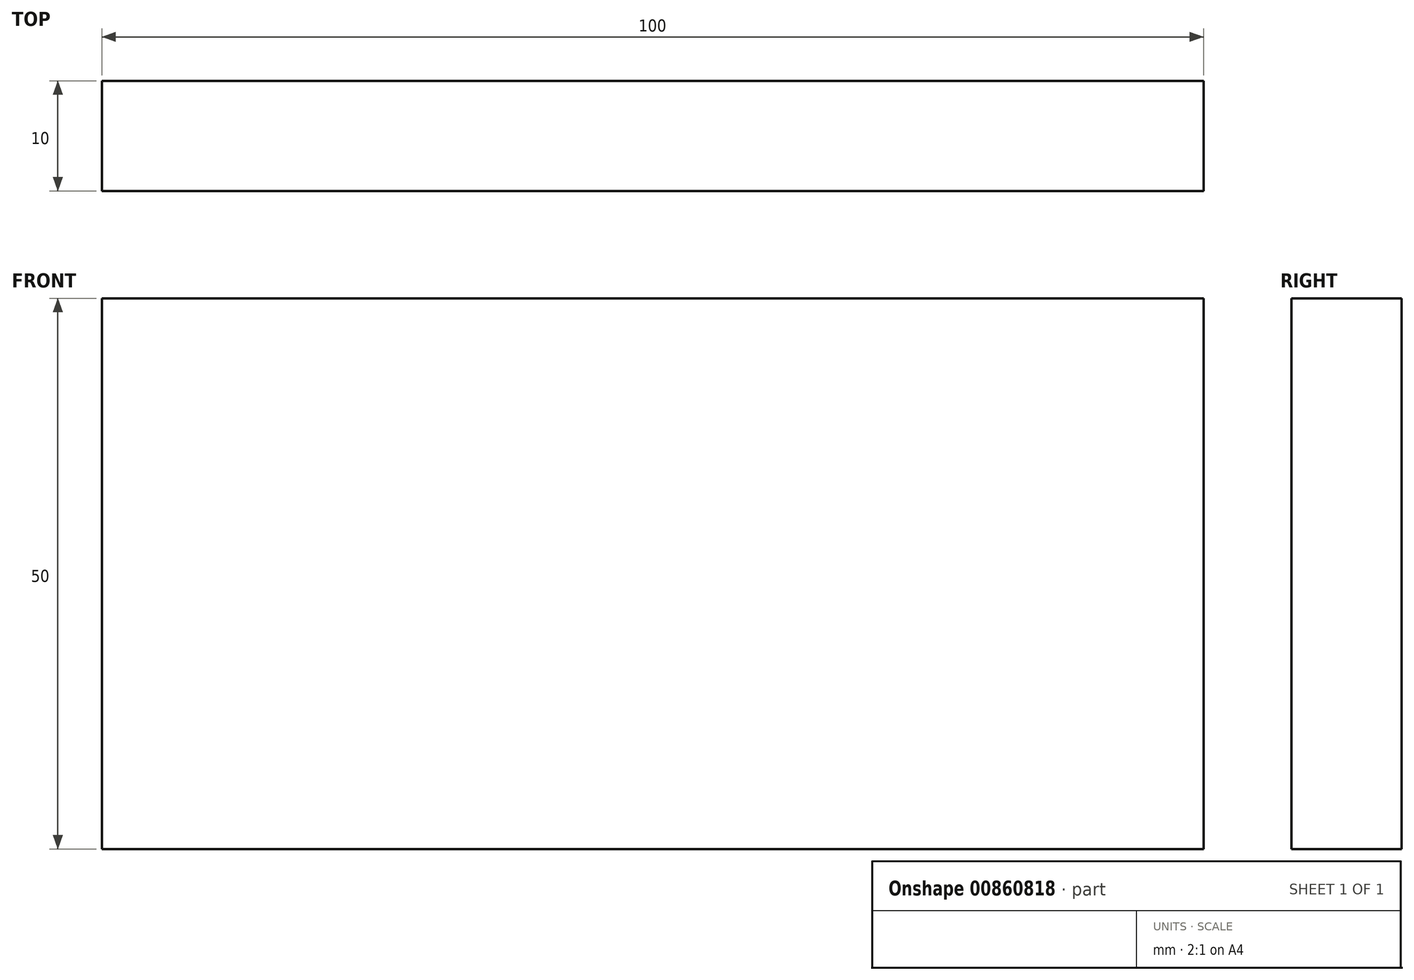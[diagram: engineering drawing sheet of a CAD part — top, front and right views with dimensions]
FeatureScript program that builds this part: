
annotation { "Feature Type Name" : "Feature", "Feature Type Description" : "" }
export const myFeature = defineFeature(function(context is Context, id is Id, definition is map)
    precondition{}
    {
        {
            var Q0;
            Q0=qCreatedBy(makeId("Front.planeOp"),FACE);
            var sketch = newSketch(context, id + "F0", { "sketchPlane" : qUnion([Q0])});
            skLineSegment(sketch, "E0", {"start": v(0, 0) * mm, "end": v(-46.75, 0) * mm});
            skLineSegment(sketch, "E1", {"start": v(-46.75, 0) * mm, "end": v(-46.75, 50) * mm});
            skLineSegment(sketch, "E2", {"start": v(-46.75, 50) * mm, "end": v(53.25, 50) * mm});
            skLineSegment(sketch, "E3", {"start": v(53.25, 50) * mm, "end": v(53.25, 0) * mm});
            skLineSegment(sketch, "E4", {"start": v(53.25, 0) * mm, "end": v(0, 0) * mm});
            skSolve(sketch);
        }
        {
            var Q0;
            Q0 = qSketchRegion(id + "F0", true);
            extrude(context, id + "F1", {"entities" : qUnion([Q0]), "endBound" : BoundingType.SYMMETRIC, "depth" : 10 * mm, "offsetDistance" : 25 * mm});
        }
    });
